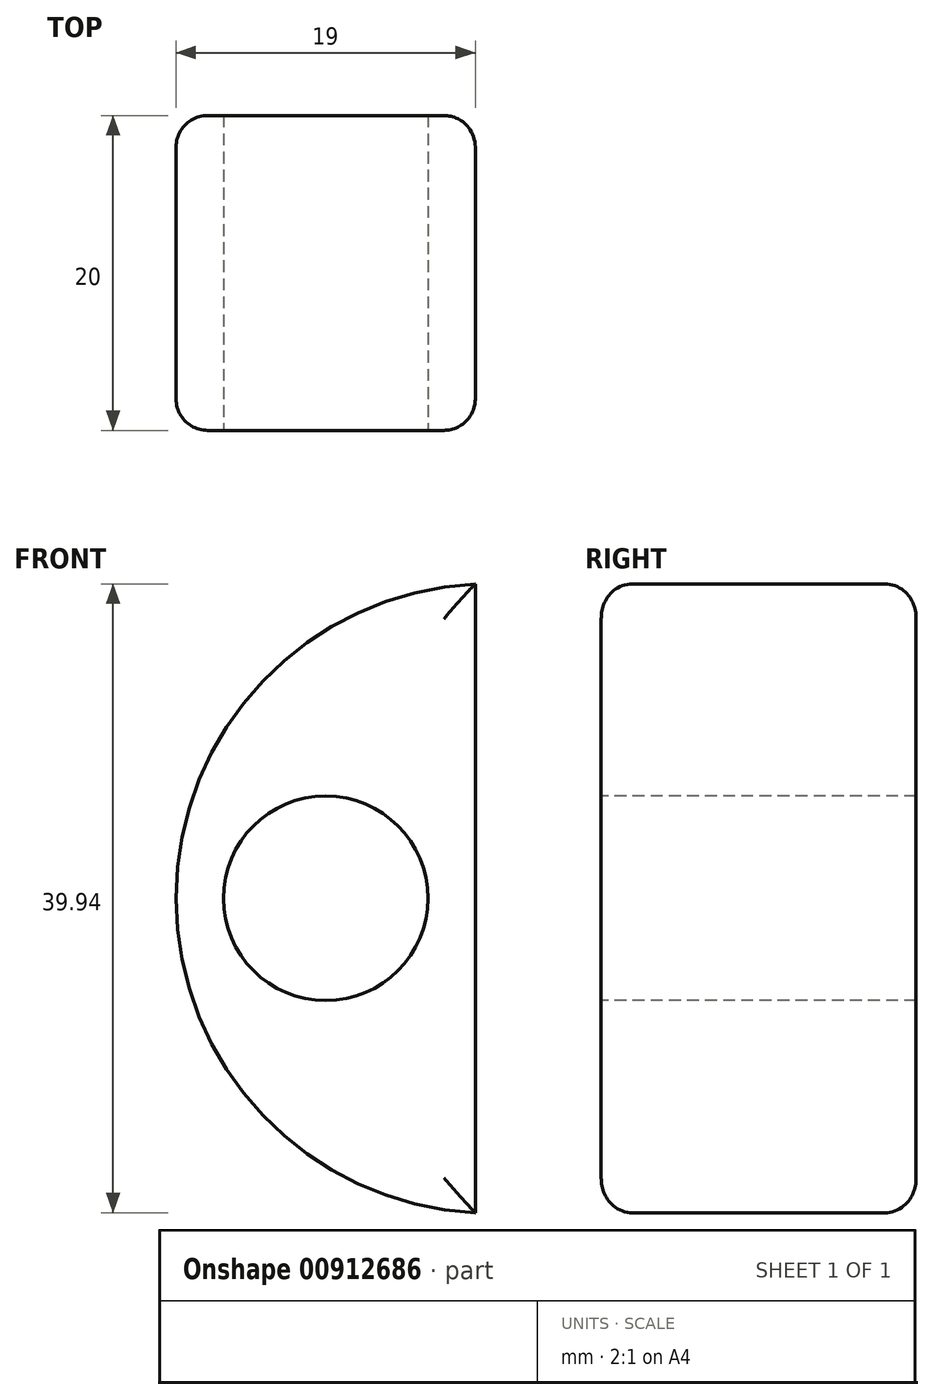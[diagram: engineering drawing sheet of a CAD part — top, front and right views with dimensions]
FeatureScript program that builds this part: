
annotation { "Feature Type Name" : "Feature", "Feature Type Description" : "" }
export const myFeature = defineFeature(function(context is Context, id is Id, definition is map)
    precondition{}
    {
        {
            var Q0;
            Q0=qCreatedBy(makeId("Front.planeOp"),FACE);
            var sketch = newSketch(context, id + "F0", { "sketchPlane" : qUnion([Q0])});
            skCircle(sketch, "E0", {"center": v(0, 0) * mm, "radius": 20 * mm});
            skLineSegment(sketch, "E1", {"start": v(0, 0.58) * mm, "end": v(0, 20) * mm});
            skLineSegment(sketch, "E2", {"start": v(0, 20) * mm, "end": v(0, -20) * mm});
            skLineSegment(sketch, "E3", {"start": v(-20, 0) * mm, "end": v(-1, 0) * mm, "construction": true});
            skLineSegment(sketch, "E4", {"start": v(-1, 0) * mm, "end": v(-1, 19.97) * mm});
            skLineSegment(sketch, "E5", {"start": v(-1, 0) * mm, "end": v(-1, -19.97) * mm});
            skSolve(sketch);
        }
        {
            var Q0;
            {var subQ0=sQuery(id+"F0.wireOp",EDGE,"E4");Q0=makeQuery(id+"F0.imprint","IMPRINT",FACE,{"disambiguationData":[TD([[makeQuery(id+"F0.imprint","IMPRINT",EDGE,{"derivedFrom":subQ0}),1.0]])]});}
            extrude(context, id + "F1", {"entities" : qUnion([Q0]), "depth" : 20 * mm, "offsetDistance" : 25 * mm});
        }
        {
            var Q0;
            Q0=makeQuery(id+"F1.opExtrude","CAP_FACE",FACE,{"disambiguationData":[OSD([sQuery(id+"F0.wireOp",EDGE,"E0"),sQuery(id+"F0.wireOp",EDGE,"E4"),sQuery(id+"F0.wireOp",EDGE,"E5")])],"isStart":false});
            var sketch = newSketch(context, id + "F2", { "sketchPlane" : qUnion([Q0])});
            skCircle(sketch, "E6", {"center": v(-10.5, 0) * mm, "radius": 6.5 * mm});
            skPoint(sketch, "E6.centerSnap0", {"position": v(-1, 0) * mm});
            skSolve(sketch);
        }
        {
            var Q0;
            Q0=makeQuery(id+"F2.imprint","IMPRINT",FACE,{"disambiguationData":[TD([[makeQuery(id+"F2.imprint","IMPRINT",EDGE,{"derivedFrom":sQuery(id+"F2.wireOp",EDGE,"E6")}),1.0]])]});
            extrude(context, id + "F3", {"entities" : qUnion([Q0]), "operationType" : NewBodyOperationType.REMOVE, "oppositeDirection" : true, "depth" : 20 * mm, "offsetDistance" : 25 * mm});
        }
        {
            var Q0;
            Q0=makeQuery(id+"F1.opExtrude","CAP_EDGE",EDGE,{"disambiguationData":[OSD([sQuery(id+"F0.wireOp",EDGE,"E0")])],"isStart":false});
            var Q1;
            Q1=makeQuery(id+"F1.opExtrude","CAP_EDGE",EDGE,{"disambiguationData":[OSD([sQuery(id+"F0.wireOp",EDGE,"E4"),sQuery(id+"F0.wireOp",EDGE,"E5")])],"isStart":false});
            var Q2;
            Q2=makeQuery(id+"F1.opExtrude","CAP_EDGE",EDGE,{"disambiguationData":[OSD([sQuery(id+"F0.wireOp",EDGE,"E0")])],"isStart":true});
            var Q3;
            Q3=makeQuery(id+"F1.opExtrude","CAP_EDGE",EDGE,{"disambiguationData":[OSD([sQuery(id+"F0.wireOp",EDGE,"E4"),sQuery(id+"F0.wireOp",EDGE,"E5")])],"isStart":true});
            var Q4;
            Q4=makeQuery(id+"F3.boolean.opBoolean","COPY",EDGE,{"derivedFrom":makeQuery(id+"F3.opExtrude","CAP_EDGE",EDGE,{"disambiguationData":[OSD([sQuery(id+"F2.wireOp",EDGE,"E6")])],"isStart":false})});
            var Q5;
            Q5=makeQuery(id+"F3.boolean.opBoolean","COPY",EDGE,{"derivedFrom":makeQuery(id+"F3.opExtrude","CAP_EDGE",EDGE,{"disambiguationData":[OSD([sQuery(id+"F2.wireOp",EDGE,"E6")])],"isStart":true})});
            fillet(context, id + "F4", {"entities" : qUnion([Q0, Q1, Q2, Q3, Q4, Q5]), "radius" : 2 * mm, "tangentPropagation" : true, "allowEdgeOverflow" : false});
        }
    });
